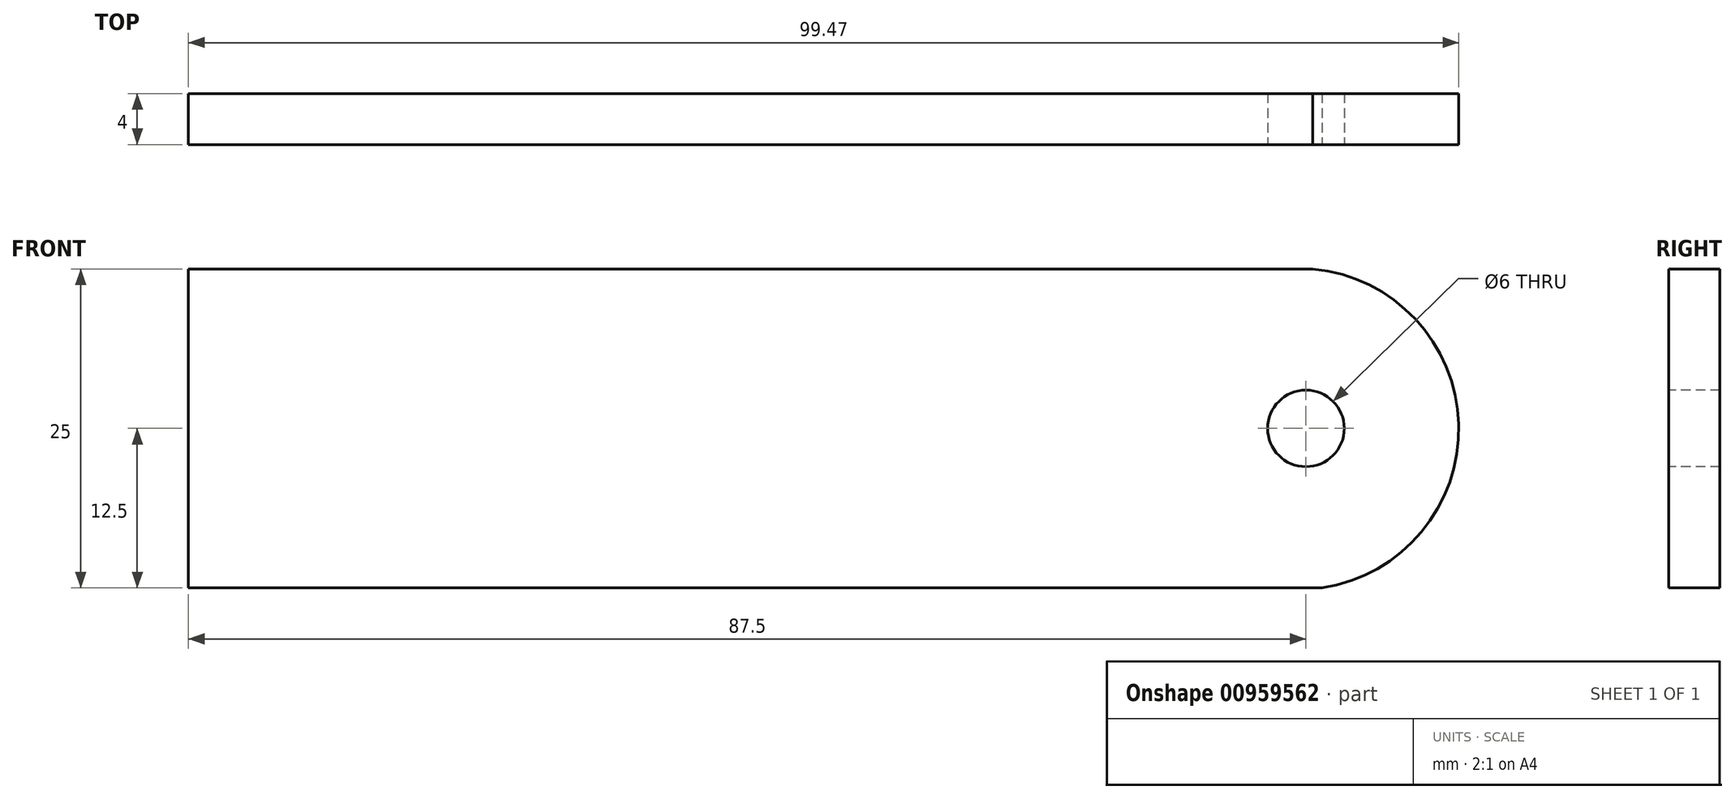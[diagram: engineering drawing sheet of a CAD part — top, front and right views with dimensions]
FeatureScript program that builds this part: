
annotation { "Feature Type Name" : "Feature", "Feature Type Description" : "" }
export const myFeature = defineFeature(function(context is Context, id is Id, definition is map)
    precondition{}
    {
        {
            var Q0;
            Q0=qCreatedBy(makeId("Front.planeOp"),FACE);
            var sketch = newSketch(context, id + "F0", { "sketchPlane" : qUnion([Q0])});
            skLineSegment(sketch, "E0.bottom", {"start": v(50, 12.5) * mm, "end": v(-50, 12.5) * mm});
            skLineSegment(sketch, "E0.top", {"start": v(50, -12.5) * mm, "end": v(-50, -12.5) * mm});
            skLineSegment(sketch, "E0.left", {"start": v(50, 12.5) * mm, "end": v(50, -12.5) * mm});
            skLineSegment(sketch, "E0.right", {"start": v(-50, 12.5) * mm, "end": v(-50, -12.5) * mm});
            skPoint(sketch, "E0.middle", {"position": v(0, 0) * mm});
            skSolve(sketch);
        }
        {
            var Q0;
            Q0=makeQuery(id+"F0.imprint","IMPRINT",FACE,{"disambiguationData":[TD([[makeQuery(id+"F0.imprint","IMPRINT",EDGE,{"derivedFrom":sQuery(id+"F0.wireOp",EDGE,"E0.bottom")}),1.0]])]});
            extrude(context, id + "F1", {"entities" : qUnion([Q0]), "depth" : 4 * mm, "offsetDistance" : 25 * mm});
        }
        {
            var Q0;
            Q0=makeQuery(id+"F1.opExtrude","CAP_FACE",FACE,{"disambiguationData":[OSD([sQuery(id+"F0.wireOp",EDGE,"E0.bottom"),sQuery(id+"F0.wireOp",EDGE,"E0.top"),sQuery(id+"F0.wireOp",EDGE,"E0.left"),sQuery(id+"F0.wireOp",EDGE,"E0.right")])],"isStart":false});
            var sketch = newSketch(context, id + "F2", { "sketchPlane" : qUnion([Q0])});
            skCircle(sketch, "E1", {"center": v(37.5, 0) * mm, "radius": 3 * mm});
            skSolve(sketch);
        }
        {
            var Q0;
            Q0=makeQuery(id+"F2.imprint","IMPRINT",FACE,{"disambiguationData":[TD([[makeQuery(id+"F2.imprint","IMPRINT",EDGE,{"derivedFrom":sQuery(id+"F2.wireOp",EDGE,"E1")}),-1.0]])]});
            var sketch = newSketch(context, id + "F3", { "sketchPlane" : qUnion([Q0])});
            skArc(sketch, "E2", {"start": v(37.62, -12.62) * mm, "mid": v(49.47, 0.1) * mm, "end": v(37.32, 12.55) * mm});
            skSolve(sketch);
        }
        {
            var Q0;
            {var subQ5=makeQuery(id+"F2.imprint","IMPRINT",EDGE,{"derivedFrom":makeQuery(id+"F1.opExtrude","CAP_EDGE",EDGE,{"disambiguationData":[OSD([sQuery(id+"F0.wireOp",EDGE,"E0.left")])],"isStart":false})});Q0=makeQuery(id+"F3.imprint","IMPRINT",FACE,{"disambiguationData":[TD([[makeQuery(id+"F3.imprint","IMPRINT",EDGE,{"derivedFrom":subQ5}),-1.0]])]});}
            extrude(context, id + "F4", {"entities" : qUnion([Q0]), "operationType" : NewBodyOperationType.REMOVE, "endBound" : BoundingType.THROUGH_ALL, "oppositeDirection" : true, "depth" : 25 * mm, "offsetDistance" : 25 * mm});
        }
        {
            var Q0;
            Q0=makeQuery(id+"F2.imprint","IMPRINT",FACE,{"disambiguationData":[TD([[makeQuery(id+"F2.imprint","IMPRINT",EDGE,{"derivedFrom":sQuery(id+"F2.wireOp",EDGE,"E1")}),1.0]])]});
            extrude(context, id + "F5", {"entities" : qUnion([Q0]), "operationType" : NewBodyOperationType.REMOVE, "endBound" : BoundingType.THROUGH_ALL, "oppositeDirection" : true, "depth" : 25 * mm, "offsetDistance" : 25 * mm});
        }
    });
